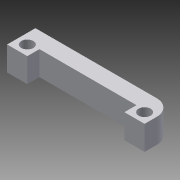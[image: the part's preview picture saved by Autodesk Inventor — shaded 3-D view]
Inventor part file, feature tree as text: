
AUTODESK INVENTOR PART (.ipt)
format: ipt  version: 2013 (Build 170138000, 138)  size: 88,576 bytes
history: native  units: mm
features: extrude x1, sketch x1
ambient origin geometry x8: Origin, YZ Plane, XZ Plane, XY Plane, X Axis, Y Axis, Z Axis, Center Point
bodies: Solid1 (feature_tree)
feature tree (2):
  extrude  "Extrusion1"  [1 undecoded]
  sketch  "Sketch1"  dims[d0=6.0mm d1=0.0mm]
note: 1 required parameter value undecoded (feature->parameter linkage not recoverable at this tier; creation-order binding heuristic only, values carry confidence <= 0.55)
